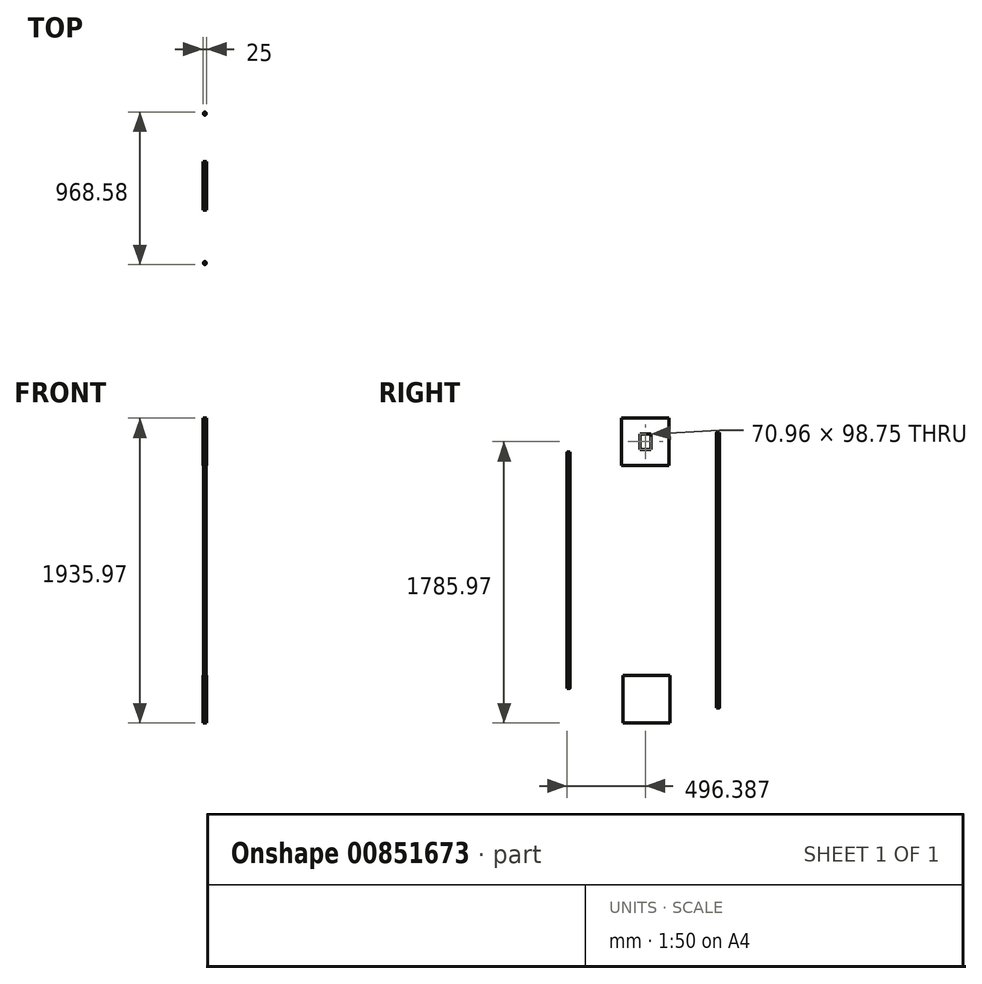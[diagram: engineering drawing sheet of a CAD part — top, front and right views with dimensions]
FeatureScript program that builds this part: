
annotation { "Feature Type Name" : "Feature", "Feature Type Description" : "" }
export const myFeature = defineFeature(function(context is Context, id is Id, definition is map)
    precondition{}
    {
        {
            var Q0;
            Q0=qCreatedBy(makeId("Top.planeOp"),FACE);
            var sketch = newSketch(context, id + "F0", { "sketchPlane" : qUnion([Q0])});
            skCircle(sketch, "E0", {"center": v(0, 0) * mm, "radius": 241.3 * mm});
            skSolve(sketch);
        }
        {
            var Q0;
            Q0=sQuery(id+"F0.wireOp",EDGE,"hlJuaxei-ZoV3-3eNb-yzud-l6tzfUNC2Mim");
            var Q1;
            Q1=sQuery(id+"F0.wireOp",EDGE,"E0");
            extrude(context, id + "F1", {"bodyType" : ToolBodyType.SURFACE, "surfaceEntities" : qUnion([Q0, Q1]), "endBound" : BoundingType.SYMMETRIC, "depth" : 185 * mm, "offsetDistance" : 25 * mm});
        }
        {
            var Q0;
            Q0=qCreatedBy(makeId("Top.planeOp"),FACE);
            var sketch = newSketch(context, id + "F2", { "sketchPlane" : qUnion([Q0])});
            skCircle(sketch, "E1", {"center": v(0, 0) * mm, "radius": 9.5 * mm});
            skSolve(sketch);
        }
        {
            var Q0;
            Q0=makeQuery(id+"F2.imprint","IMPRINT",FACE,{"disambiguationData":[TD([[makeQuery(id+"F2.imprint","IMPRINT",EDGE,{"derivedFrom":sQuery(id+"F2.wireOp",EDGE,"E1")}),1.0]])]});
            var Q1;
            Q1=sQuery(id+"F2.wireOp",EDGE,"E1");
            extrude(context, id + "F3", {"entities" : qUnion([Q0]), "surfaceEntities" : qUnion([Q1]), "oppositeDirection" : true, "depth" : 1500 * mm, "offsetDistance" : 25 * mm});
        }
        {
            var Q0;
            Q0=makeQuery(id+"F3.opExtrude","CAP_FACE",FACE,{"disambiguationData":[OSD([sQuery(id+"F2.wireOp",EDGE,"E1")])],"isStart":false});
            var sketch = newSketch(context, id + "F4", { "sketchPlane" : qUnion([Q0])});
            skCircle(sketch, "E2", {"center": v(0, 0) * mm, "radius": 241.3 * mm});
            skSolve(sketch);
        }
        {
            var Q0;
            Q0 = qSketchRegion(id + "F4", true);
            var Q1;
            Q1=sQuery(id+"F4.wireOp",EDGE,"E2");
            extrude(context, id + "F5", {"entities" : qUnion([Q0]), "bodyType" : ToolBodyType.SURFACE, "surfaceEntities" : qUnion([Q1]), "endBound" : BoundingType.SYMMETRIC, "depth" : 185 * mm, "offsetDistance" : 25 * mm});
        }
        {
            var Q0;
            Q0=qCreatedBy(makeId("Top.planeOp"),FACE);
            cPlane(context, id + "F6", {"entities" : qUnion([Q0]), "cplaneType" : CPlaneType.OFFSET, "offset" : 125 * mm, "width" : 150 * mm, "height" : 150 * mm});
        }
        {
            var Q0;
            Q0=qCreatedBy(id+"F6.planeOp",FACE);
            var sketch = newSketch(context, id + "F7", { "sketchPlane" : qUnion([Q0])});
            skCircle(sketch, "E3", {"center": v(0, 955.76) * mm, "radius": 241.3 * mm});
            skSolve(sketch);
        }
        {
            var Q0;
            Q0 = qSketchRegion(id + "F7", true);
            var Q1;
            Q1=sQuery(id+"F7.wireOp",EDGE,"E3");
            extrude(context, id + "F8", {"entities" : qUnion([Q0]), "bodyType" : ToolBodyType.SURFACE, "surfaceEntities" : qUnion([Q1]), "endBound" : BoundingType.SYMMETRIC, "depth" : 195 * mm, "offsetDistance" : 25 * mm});
        }
        {
            var Q0;
            Q0=qCreatedBy(id+"F6.planeOp",FACE);
            var sketch = newSketch(context, id + "F9", { "sketchPlane" : qUnion([Q0])});
            skCircle(sketch, "E4", {"center": v(0, 949.58) * mm, "radius": 9.5 * mm});
            skSolve(sketch);
        }
        {
            var Q0;
            Q0 = qSketchRegion(id + "F9", true);
            extrude(context, id + "F10", {"entities" : qUnion([Q0]), "oppositeDirection" : true, "depth" : 1750 * mm, "offsetDistance" : 25 * mm});
        }
        {
            var Q0;
            Q0=makeQuery(id+"F10.opExtrude","CAP_FACE",FACE,{"disambiguationData":[OSD([sQuery(id+"F9.wireOp",EDGE,"E4")])],"isStart":false});
            var sketch = newSketch(context, id + "F11", { "sketchPlane" : qUnion([Q0])});
            skCircle(sketch, "E5", {"center": v(0, -949.58) * mm, "radius": 241.3 * mm});
            skSolve(sketch);
        }
        {
            var Q0;
            Q0 = qSketchRegion(id + "F11", true);
            var Q1;
            Q1=sQuery(id+"F11.wireOp",EDGE,"E5");
            extrude(context, id + "F12", {"entities" : qUnion([Q0]), "bodyType" : ToolBodyType.SURFACE, "operationType" : NewBodyOperationType.ADD, "surfaceEntities" : qUnion([Q1]), "endBound" : BoundingType.SYMMETRIC, "depth" : 195 * mm, "offsetDistance" : 25 * mm});
        }
        {
            var Q0;
            Q0=qCreatedBy(makeId("Right.planeOp"),FACE);
            var sketch = newSketch(context, id + "F13", { "sketchPlane" : qUnion([Q0])});
            skLineSegment(sketch, "E6.bottom", {"start": v(636.89, 215.78) * mm, "end": v(336.89, 215.78) * mm});
            skLineSegment(sketch, "E6.top", {"start": v(636.89, -84.22) * mm, "end": v(336.89, -84.22) * mm});
            skLineSegment(sketch, "E6.left", {"start": v(636.89, 215.78) * mm, "end": v(636.89, -84.22) * mm});
            skLineSegment(sketch, "E6.right", {"start": v(336.89, 215.78) * mm, "end": v(336.89, -84.22) * mm});
            skPoint(sketch, "E6.middle", {"position": v(486.89, 65.78) * mm});
            skLineSegment(sketch, "E7.bottom", {"start": v(522.37, 16.4) * mm, "end": v(451.4, 16.4) * mm});
            skLineSegment(sketch, "E7.top", {"start": v(522.37, 115.16) * mm, "end": v(451.4, 115.16) * mm});
            skLineSegment(sketch, "E7.left", {"start": v(522.37, 16.4) * mm, "end": v(522.37, 115.16) * mm});
            skLineSegment(sketch, "E7.right", {"start": v(451.4, 16.4) * mm, "end": v(451.4, 115.16) * mm});
            skSolve(sketch);
        }
        {
            var Q0;
            Q0 = qSketchRegion(id + "F13", true);
            extrude(context, id + "F14", {"entities" : qUnion([Q0]), "endBound" : BoundingType.SYMMETRIC, "depth" : 25 * mm, "offsetDistance" : 25 * mm});
        }
        {
            var Q0;
            Q0=qCreatedBy(makeId("Right.planeOp"),FACE);
            var sketch = newSketch(context, id + "F15", { "sketchPlane" : qUnion([Q0])});
            skLineSegment(sketch, "E8.bottom", {"start": v(643.33, -1420.2) * mm, "end": v(343.33, -1420.2) * mm});
            skLineSegment(sketch, "E8.top", {"start": v(643.33, -1720.2) * mm, "end": v(343.33, -1720.2) * mm});
            skLineSegment(sketch, "E8.left", {"start": v(643.33, -1420.2) * mm, "end": v(643.33, -1720.2) * mm});
            skLineSegment(sketch, "E8.right", {"start": v(343.33, -1420.2) * mm, "end": v(343.33, -1720.2) * mm});
            skPoint(sketch, "E8.middle", {"position": v(493.33, -1570.2) * mm});
            skSolve(sketch);
        }
        {
            var Q0;
            Q0=makeQuery(id+"F15.imprint","IMPRINT",FACE,{"disambiguationData":[TD([[makeQuery(id+"F15.imprint","IMPRINT",EDGE,{"derivedFrom":sQuery(id+"F15.wireOp",EDGE,"E8.bottom")}),1.0]])]});
            extrude(context, id + "F16", {"entities" : qUnion([Q0]), "endBound" : BoundingType.SYMMETRIC, "depth" : 25 * mm, "offsetDistance" : 25 * mm});
        }
    });
